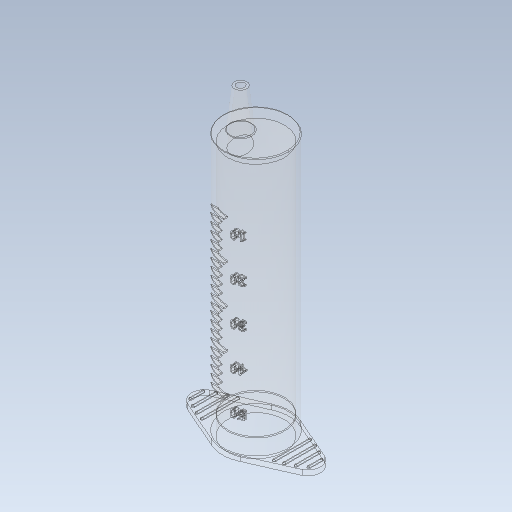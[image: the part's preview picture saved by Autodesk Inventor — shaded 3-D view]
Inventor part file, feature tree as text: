
AUTODESK INVENTOR PART (.ipt)
format: ipt  version: 2020 (Build 240168000, 168)  size: 848,384 bytes
history: native  units: mm
features: sketch x9, extrude x6, plane x4, revolve x3, fillet x2, loft x1, mirror x1, other x1
ambient origin geometry x8: Origin, YZ Plane, XZ Plane, XY Plane, X Axis, Y Axis, Z Axis, Center Point
bodies: Solid1 (feature_tree)
feature tree (27):
  revolve  "Revolution1"  [1 undecoded]
  plane  "Work Plane1"
  loft  "Loft1"
  extrude  "Extrusion1"  Depth=4.0mm
  plane  "Work Plane2"
  revolve  "Revolution2"  Angle=90.0deg
  revolve  "Revolution3"  [1 undecoded]
  fillet  "Fillet1"  Radius=13.0mm
  extrude  "Extrusion2"  Depth=7.0mm
  extrude  "Extrusion3"  Depth=11.0mm
  plane  "Work Plane3"
  extrude  "Extrusion4"  TaperAngle=360.0deg  [1 undecoded]
  extrude  "Extrusion5"  Depth=1.047198mm
  extrude  "Extrusion7"  Depth=0.5mm
  fillet  "Fillet2"  Radius=2.0mm
  mirror  "Mirror1"
  sketch  "Sketch1"  dims[d0=100.0mm d1=2.0mm]
  sketch  "Sketch2"  dims[d2=13.0mm d3=12.5mm]
  other  "Edges1"
  sketch  "Sketch3"  dims[d4=90.0deg d5=4.0mm]
  sketch  "Sketch4"  dims[d7=8.0mm d8=0.0mm d9=90.0deg]
  sketch  "Sketch5"  dims[d10=0.0mm d11=90.0deg d12=15.0mm d13=-1.047198mm d14=13.0mm]
  sketch  "Sketch7"  dims[d15=11.0mm d16=7.0mm]
  sketch  "Sketch8"  dims[d17=0.5mm d18=11.0mm]
  sketch  "Sketch9"  dims[d19=12.217305mm d20=360.0deg]
  sketch  "Sketch11"  dims[d22=90.0deg d24=1.047198mm d25=0.5mm d28=2.0mm d29=0.0mm d30=22.0mm d31=2.0mm d32=0.0mm d33=15.0mm d35=7.5mm d36=0.5mm d38=2.5mm d39=7.5mm d40=2.5mm d41=0.5mm d42=200.0mm d44=3.0mm d45=10.0mm d47=10.0mm d49=50.0mm d51=15.0mm d52=10.0mm d54=10.0mm d56=5.0mm d57=0.0mm d60=5.0mm d61=2.25mm d62=50.0mm d64=15.0mm d65=10.0mm d67=10.0mm d69=5.0mm d70=0.0mm d104=7.0mm d105=7.0mm d106=0.5mm d107=3.0mm d108=6.0mm d109=6.0mm d110=0.5mm d111=3.0mm d112=4.5mm d113=4.5mm d114=0.5mm d115=3.0mm d116=2.5mm d117=2.5mm d118=0.5mm d119=0.75mm d120=0.0mm d121=0.5mm]
  plane  "Work Plane4"
note: 3 required parameter values undecoded (feature->parameter linkage not recoverable at this tier; creation-order binding heuristic only, values carry confidence <= 0.55)